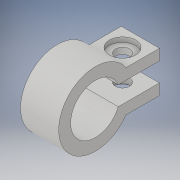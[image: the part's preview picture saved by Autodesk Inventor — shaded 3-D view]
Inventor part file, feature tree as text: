
AUTODESK INVENTOR PART (.ipt)
format: ipt  version: 2019 (Build 230136000, 136)  size: 150,016 bytes
history: native  units: in
note: dims shown in document units (in); Inventor stores cm internally (conversion verified against a paired STEP export)
features: extrude x3, sketch x3, projected_geometry x3, mirror x1
ambient origin geometry x8: Origin, YZ Plane, XZ Plane, XY Plane, X Axis, Y Axis, Z Axis, Center Point
bodies: Solid1 (feature_tree)
feature tree (10):
  extrude  "Extrusion1"  Depth=0.0984in
  extrude  "Extrusion2"  Depth=0.2362in
  extrude  "Extrusion3"  TaperAngle=90.0deg  [1 undecoded]
  mirror  "Mirror1"
  sketch  "Sketch2"  dims[d6=0.4094in d7=0.0984in]
  sketch  "Sketch3"  dims[d9=0.0787in d10=0.2362in]
  projected_geometry  "Projected Loop1"
  sketch  "Sketch4"  dims[d11=0.0906in d12=90.0deg d13=0.315in d14=0.0in d15=0.1181in d16=0.315in d17=0.0in d18=0.2165in d19=0.0394in d20=0.0in d21=0.1299in]
  projected_geometry  "Projected Loop2"
  projected_geometry  "Projected Loop3"
note: 1 required parameter value undecoded (feature->parameter linkage not recoverable at this tier; creation-order binding heuristic only, values carry confidence <= 0.55)
